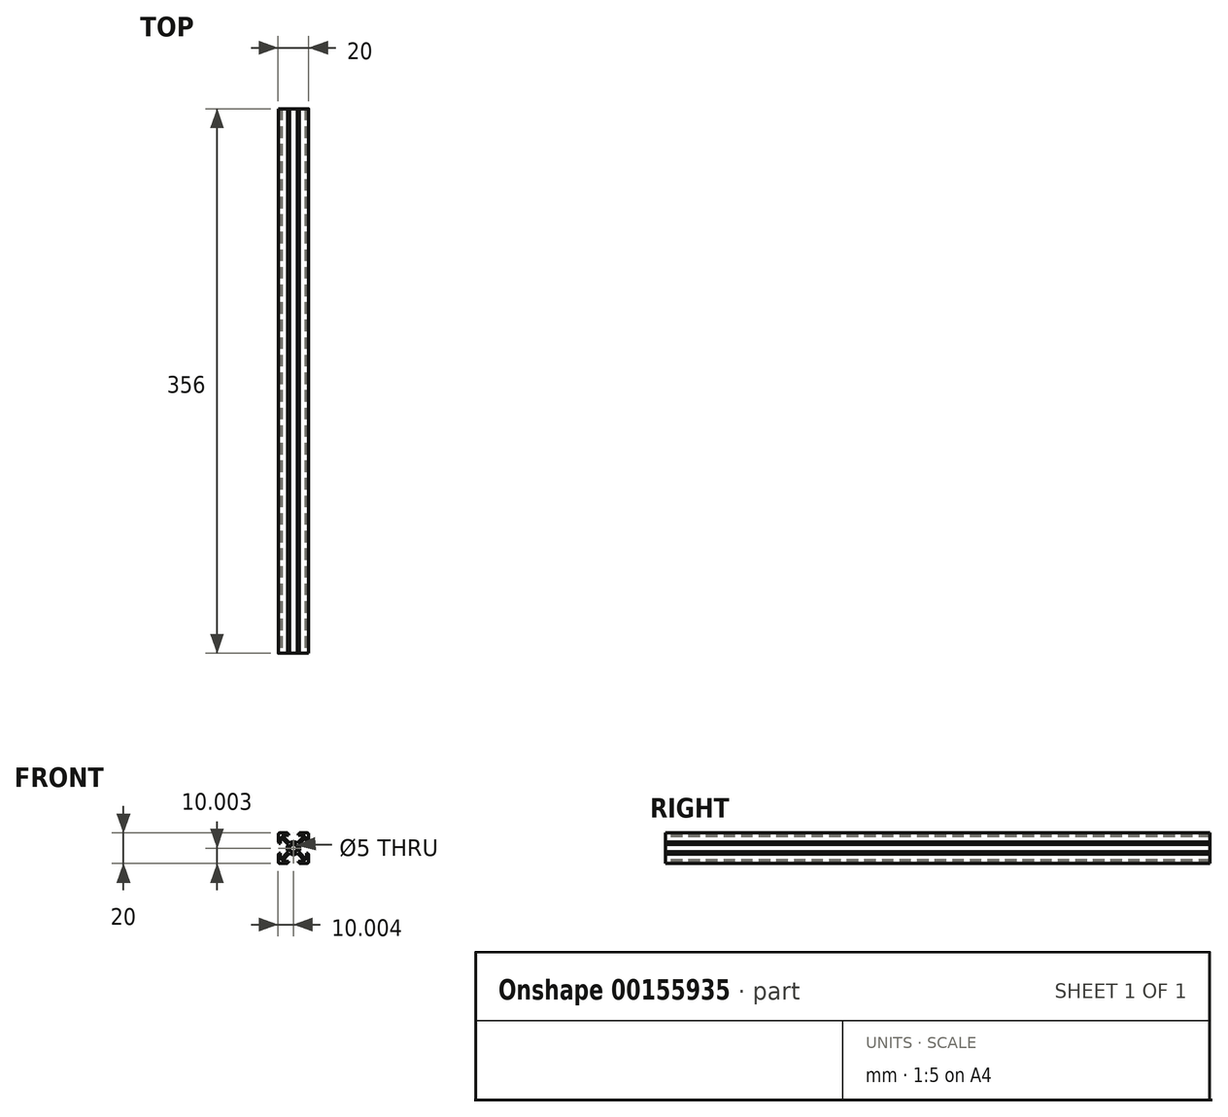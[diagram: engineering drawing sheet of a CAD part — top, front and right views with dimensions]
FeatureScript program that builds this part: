
annotation { "Feature Type Name" : "Feature", "Feature Type Description" : "" }
export const myFeature = defineFeature(function(context is Context, id is Id, definition is map)
    precondition{}
    {
        {
            var Q0;
            Q0=qCreatedBy(makeId("Front.planeOp"),FACE);
            var sketch = newSketch(context, id + "F0", { "sketchPlane" : qUnion([Q0])});
            skArc(sketch, "E0", {"start": v(-44.98, 42.64) * mm, "mid": v(-45.76, 40.2) * mm, "end": v(-44.98, 37.77) * mm});
            skCircle(sketch, "E1", {"center": v(-41.56, 40.2) * mm, "radius": 2.5 * mm});
            skLineSegment(sketch, "E2", {"start": v(-54.61, 53.26) * mm, "end": v(-41.56, 40.2) * mm, "construction": true});
            skLineSegment(sketch, "E3", {"start": v(-41.56, 40.2) * mm, "end": v(-28.67, 27.32) * mm, "construction": true});
            skLineSegment(sketch, "E4", {"start": v(-41.56, 40.2) * mm, "end": v(-29.82, 51.94) * mm, "construction": true});
            skLineSegment(sketch, "E5", {"start": v(-41.56, 40.2) * mm, "end": v(-53.14, 28.61) * mm, "construction": true});
            skLineSegment(sketch, "E6", {"start": v(-55.54, 40.2) * mm, "end": v(-21.72, 40.2) * mm, "construction": true});
            skLineSegment(sketch, "E7", {"start": v(-41.56, 50.17) * mm, "end": v(-41.56, 24.27) * mm, "construction": true});
            skLineSegment(sketch, "E8", {"start": v(-50.36, 50.2) * mm, "end": v(-45.5, 50.2) * mm});
            skLineSegment(sketch, "E9", {"start": v(-44.76, 49.6) * mm, "end": v(-44.76, 48.8) * mm});
            skLineSegment(sketch, "E10", {"start": v(-49.17, 48.8) * mm, "end": v(-43.99, 43.63) * mm});
            skLineSegment(sketch, "E11", {"start": v(-44.76, 48.8) * mm, "end": v(-49.17, 48.8) * mm});
            skLineSegment(sketch, "E12", {"start": v(-45.5, 50.2) * mm, "end": v(-45.5, 49.6) * mm});
            skLineSegment(sketch, "E13", {"start": v(-45.5, 49.6) * mm, "end": v(-44.76, 49.6) * mm});
            skPoint(sketch, "E14.orphan", {"position": v(-44.76, 50.2) * mm});
            skLineSegment(sketch, "E15.MirrorCS", {"start": v(-50.16, 47.81) * mm, "end": v(-44.98, 42.64) * mm});
            skLineSegment(sketch, "E16.MirrorCS", {"start": v(-50.16, 43.4) * mm, "end": v(-50.16, 47.81) * mm});
            skLineSegment(sketch, "E17.MirrorCS", {"start": v(-50.95, 43.4) * mm, "end": v(-50.16, 43.4) * mm});
            skLineSegment(sketch, "E18.MirrorCS", {"start": v(-50.95, 44.15) * mm, "end": v(-50.95, 43.4) * mm});
            skLineSegment(sketch, "E19.MirrorCS", {"start": v(-51.56, 49) * mm, "end": v(-51.56, 44.15) * mm});
            skLineSegment(sketch, "E20.MirrorCS", {"start": v(-51.56, 44.15) * mm, "end": v(-50.95, 44.15) * mm});
            skLineSegment(sketch, "E21.MirrorCS", {"start": v(-32.96, 47.81) * mm, "end": v(-38.13, 42.64) * mm});
            skLineSegment(sketch, "E22.MirrorCS", {"start": v(-33.95, 48.8) * mm, "end": v(-39.12, 43.63) * mm});
            skLineSegment(sketch, "E23.MirrorCS", {"start": v(-37.6, 49.6) * mm, "end": v(-38.36, 49.6) * mm});
            skLineSegment(sketch, "E24.MirrorCS", {"start": v(-32.16, 44.15) * mm, "end": v(-32.16, 43.4) * mm});
            skLineSegment(sketch, "E25.MirrorCS", {"start": v(-31.56, 44.15) * mm, "end": v(-32.16, 44.15) * mm});
            skLineSegment(sketch, "E26.MirrorCS", {"start": v(-38.36, 49.6) * mm, "end": v(-38.36, 48.8) * mm});
            skLineSegment(sketch, "E27.MirrorCS", {"start": v(-37.6, 50.2) * mm, "end": v(-37.6, 49.6) * mm});
            skLineSegment(sketch, "E28.MirrorCS", {"start": v(-32.16, 43.4) * mm, "end": v(-32.96, 43.4) * mm});
            skLineSegment(sketch, "E29.MirrorCS", {"start": v(-32.96, 43.4) * mm, "end": v(-32.96, 47.81) * mm});
            skPoint(sketch, "E30.MirrorP", {"position": v(-38.36, 50.2) * mm});
            skLineSegment(sketch, "E31.MirrorCS", {"start": v(-38.36, 48.8) * mm, "end": v(-33.95, 48.8) * mm});
            skLineSegment(sketch, "E32.MirrorCS", {"start": v(-32.76, 50.2) * mm, "end": v(-37.6, 50.2) * mm});
            skLineSegment(sketch, "E33.MirrorCS", {"start": v(-31.56, 49) * mm, "end": v(-31.56, 44.15) * mm});
            skLineSegment(sketch, "E34.MirrorCS", {"start": v(-32.16, 37) * mm, "end": v(-32.96, 37) * mm});
            skLineSegment(sketch, "E35.MirrorCS", {"start": v(-38.36, 30.8) * mm, "end": v(-38.36, 31.6) * mm});
            skLineSegment(sketch, "E36.MirrorCS", {"start": v(-32.16, 36.25) * mm, "end": v(-32.16, 37) * mm});
            skLineSegment(sketch, "E37.MirrorCS", {"start": v(-37.6, 30.8) * mm, "end": v(-38.36, 30.8) * mm});
            skLineSegment(sketch, "E38.MirrorCS", {"start": v(-31.56, 36.25) * mm, "end": v(-32.16, 36.25) * mm});
            skLineSegment(sketch, "E39.MirrorCS", {"start": v(-37.6, 30.2) * mm, "end": v(-37.6, 30.8) * mm});
            skLineSegment(sketch, "E40.MirrorCS", {"start": v(-32.76, 30.2) * mm, "end": v(-37.6, 30.2) * mm});
            skLineSegment(sketch, "E41.MirrorCS", {"start": v(-31.56, 31.4) * mm, "end": v(-31.56, 36.25) * mm});
            skLineSegment(sketch, "E42.MirrorCS", {"start": v(-33.95, 31.6) * mm, "end": v(-39.12, 36.78) * mm});
            skLineSegment(sketch, "E43.MirrorCS", {"start": v(-32.96, 37) * mm, "end": v(-32.96, 32.6) * mm});
            skPoint(sketch, "E44.MirrorP", {"position": v(-38.36, 30.2) * mm});
            skLineSegment(sketch, "E45.MirrorCS", {"start": v(-38.36, 31.6) * mm, "end": v(-33.95, 31.6) * mm});
            skLineSegment(sketch, "E46.MirrorCS", {"start": v(-32.96, 32.6) * mm, "end": v(-38.13, 37.77) * mm});
            skLineSegment(sketch, "E47.MirrorCS", {"start": v(-45.5, 30.8) * mm, "end": v(-44.76, 30.8) * mm});
            skLineSegment(sketch, "E48.MirrorCS", {"start": v(-51.56, 36.25) * mm, "end": v(-50.95, 36.25) * mm});
            skLineSegment(sketch, "E49.MirrorCS", {"start": v(-50.95, 36.25) * mm, "end": v(-50.95, 37) * mm});
            skLineSegment(sketch, "E50.MirrorCS", {"start": v(-50.95, 37) * mm, "end": v(-50.16, 37) * mm});
            skLineSegment(sketch, "E51.MirrorCS", {"start": v(-45.5, 30.2) * mm, "end": v(-45.5, 30.8) * mm});
            skLineSegment(sketch, "E52.MirrorCS", {"start": v(-44.76, 30.8) * mm, "end": v(-44.76, 31.6) * mm});
            skLineSegment(sketch, "E53.MirrorCS", {"start": v(-50.16, 37) * mm, "end": v(-50.16, 32.6) * mm});
            skLineSegment(sketch, "E54.MirrorCS", {"start": v(-50.16, 32.6) * mm, "end": v(-44.98, 37.77) * mm});
            skLineSegment(sketch, "E55.MirrorCS", {"start": v(-50.36, 30.2) * mm, "end": v(-45.5, 30.2) * mm});
            skPoint(sketch, "E56.MirrorP", {"position": v(-44.76, 30.2) * mm});
            skLineSegment(sketch, "E57.MirrorCS", {"start": v(-51.56, 31.4) * mm, "end": v(-51.56, 36.25) * mm});
            skLineSegment(sketch, "E58.MirrorCS", {"start": v(-49.17, 31.6) * mm, "end": v(-43.99, 36.78) * mm});
            skLineSegment(sketch, "E59.MirrorCS", {"start": v(-44.76, 31.6) * mm, "end": v(-49.17, 31.6) * mm});
            skPoint(sketch, "E60.visualSharp", {"position": v(-51.56, 50.2) * mm});
            skArc(sketch, "E60.filletArc", {"start": v(-50.36, 50.2) * mm, "mid": v(-51.2, 49.85) * mm, "end": v(-51.56, 49) * mm});
            skPoint(sketch, "E61.visualSharp", {"position": v(-31.56, 50.2) * mm});
            skArc(sketch, "E61.filletArc", {"start": v(-31.56, 49) * mm, "mid": v(-31.9, 49.85) * mm, "end": v(-32.76, 50.2) * mm});
            skPoint(sketch, "E62.visualSharp", {"position": v(-31.56, 30.2) * mm});
            skArc(sketch, "E62.filletArc", {"start": v(-32.76, 30.2) * mm, "mid": v(-31.9, 30.55) * mm, "end": v(-31.56, 31.4) * mm});
            skPoint(sketch, "E63.visualSharp", {"position": v(-51.56, 30.2) * mm});
            skArc(sketch, "E63.filletArc", {"start": v(-51.56, 31.4) * mm, "mid": v(-51.2, 30.55) * mm, "end": v(-50.36, 30.2) * mm});
            skArc(sketch, "E64.trimOffspring", {"start": v(-39.12, 43.63) * mm, "mid": v(-41.56, 44.4) * mm, "end": v(-43.99, 43.63) * mm});
            skArc(sketch, "E65.trimOffspring", {"start": v(-43.99, 36.78) * mm, "mid": v(-41.56, 36) * mm, "end": v(-39.12, 36.78) * mm});
            skArc(sketch, "E66.trimOffspring", {"start": v(-38.13, 37.77) * mm, "mid": v(-37.36, 40.2) * mm, "end": v(-38.13, 42.64) * mm});
            skSolve(sketch);
        }
        {
            var Q0;
            Q0=makeQuery(id+"F0.imprint","IMPRINT",FACE,{"disambiguationData":[TD([[makeQuery(id+"F0.imprint","IMPRINT",EDGE,{"derivedFrom":sQuery(id+"F0.wireOp",EDGE,"E0")}),1.0]])]});
            extrude(context, id + "F1", {"entities" : qUnion([Q0]), "oppositeDirection" : true, "depth" : 356 * mm, "offsetDistance" : 25 * mm});
        }
    });
